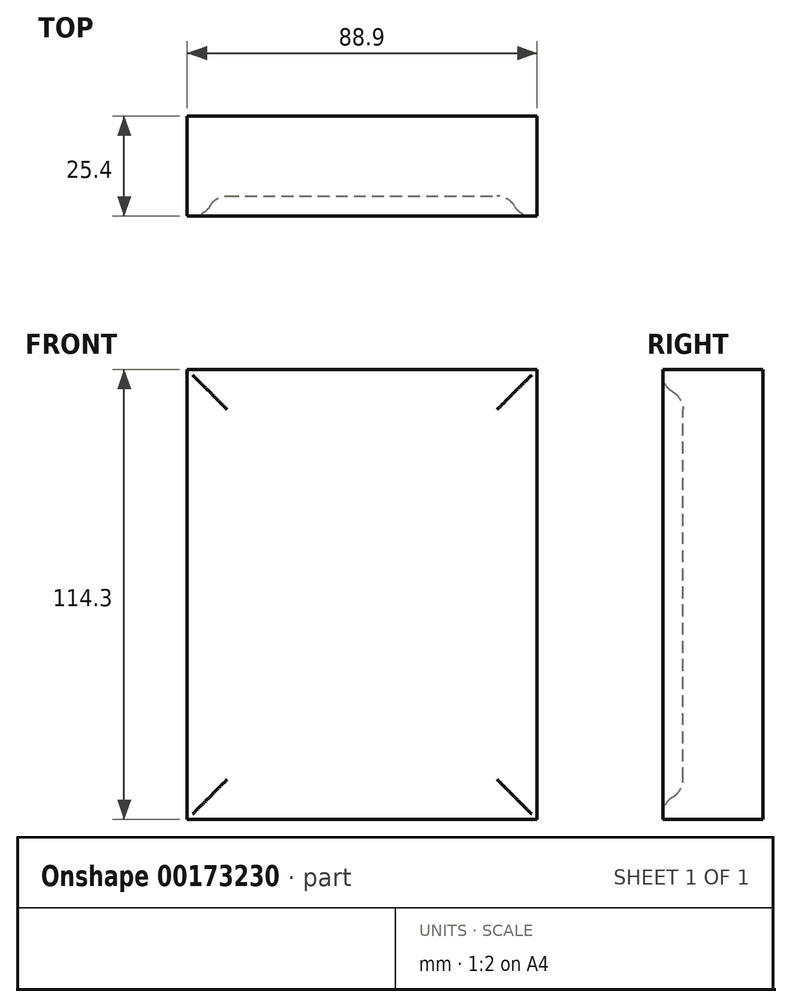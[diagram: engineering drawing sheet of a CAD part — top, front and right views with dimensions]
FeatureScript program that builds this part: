
annotation { "Feature Type Name" : "Feature", "Feature Type Description" : "" }
export const myFeature = defineFeature(function(context is Context, id is Id, definition is map)
    precondition{}
    {
        {
            var Q0;
            Q0=qCreatedBy(makeId("Front.planeOp"),FACE);
            var sketch = newSketch(context, id + "F0", { "sketchPlane" : qUnion([Q0])});
            skLineSegment(sketch, "E0.bottom", {"start": v(0, 0) * mm, "end": v(88.9, 0) * mm});
            skLineSegment(sketch, "E0.top", {"start": v(0, 114.3) * mm, "end": v(88.9, 114.3) * mm});
            skLineSegment(sketch, "E0.left", {"start": v(0, 0) * mm, "end": v(0, 114.3) * mm});
            skLineSegment(sketch, "E0.right", {"start": v(88.9, 0) * mm, "end": v(88.9, 114.3) * mm});
            skSolve(sketch);
        }
        {
            var Q0;
            Q0 = qSketchRegion(id + "F0", true);
            extrude(context, id + "F1", {"entities" : qUnion([Q0]), "depth" : 25.4 * mm});
        }
        {
            var Q0;
            Q0=makeQuery(id+"F1.opExtrude","CAP_FACE",FACE,{"disambiguationData":[OSD([sQuery(id+"F0.wireOp",EDGE,"E0.bottom"),sQuery(id+"F0.wireOp",EDGE,"E0.top"),sQuery(id+"F0.wireOp",EDGE,"E0.left"),sQuery(id+"F0.wireOp",EDGE,"E0.right")])],"isStart":false});
            var sketch = newSketch(context, id + "F2", { "sketchPlane" : qUnion([Q0])});
            skLineSegment(sketch, "E1.bottom", {"start": v(5.08, 5.08) * mm, "end": v(83.82, 5.08) * mm});
            skLineSegment(sketch, "E1.top", {"start": v(5.08, 109.22) * mm, "end": v(83.82, 109.22) * mm});
            skLineSegment(sketch, "E1.left", {"start": v(5.08, 5.08) * mm, "end": v(5.08, 109.22) * mm});
            skLineSegment(sketch, "E1.right", {"start": v(83.82, 5.08) * mm, "end": v(83.82, 109.22) * mm});
            skSolve(sketch);
        }
        {
            var Q0;
            Q0 = qSketchRegion(id + "F2", true);
            extrude(context, id + "F3", {"entities" : qUnion([Q0]), "operationType" : NewBodyOperationType.REMOVE, "oppositeDirection" : true, "depth" : 5.08 * mm});
        }
        {
            var Q0;
            Q0=makeQuery(id+"F3.boolean.opBoolean","COPY",EDGE,{"derivedFrom":makeQuery(id+"F3.opExtrude","CAP_EDGE",EDGE,{"disambiguationData":[OSD([sQuery(id+"F2.wireOp",EDGE,"E1.right")])],"isStart":false})});
            var Q1;
            Q1=makeQuery(id+"F3.boolean.opBoolean","COPY",EDGE,{"derivedFrom":makeQuery(id+"F3.opExtrude","CAP_EDGE",EDGE,{"disambiguationData":[OSD([sQuery(id+"F2.wireOp",EDGE,"E1.top")])],"isStart":false})});
            var Q2;
            Q2=makeQuery(id+"F3.boolean.opBoolean","COPY",EDGE,{"derivedFrom":makeQuery(id+"F3.opExtrude","CAP_EDGE",EDGE,{"disambiguationData":[OSD([sQuery(id+"F2.wireOp",EDGE,"E1.left")])],"isStart":false})});
            var Q3;
            Q3=makeQuery(id+"F3.boolean.opBoolean","COPY",EDGE,{"derivedFrom":makeQuery(id+"F3.opExtrude","CAP_EDGE",EDGE,{"disambiguationData":[OSD([sQuery(id+"F2.wireOp",EDGE,"E1.bottom")])],"isStart":false})});
            fillet(context, id + "F4", {"entities" : qUnion([Q0, Q1, Q2, Q3]), "radius" : 5.08 * mm, "tangentPropagation" : true, "allowEdgeOverflow" : false});
        }
        {
            var Q0;
            Q0=makeQuery(id+"F4.opFillet","BLEND_EDGE",EDGE,{"blendedFrom":[makeQuery(id+"F3.boolean.opBoolean","COPY",EDGE,{"derivedFrom":makeQuery(id+"F3.opExtrude","CAP_EDGE",EDGE,{"disambiguationData":[OSD([sQuery(id+"F2.wireOp",EDGE,"E1.left")])],"isStart":false})}),makeQuery(id+"F1.opExtrude","CAP_FACE",FACE,{"disambiguationData":[OSD([sQuery(id+"F0.wireOp",EDGE,"E0.bottom"),sQuery(id+"F0.wireOp",EDGE,"E0.top"),sQuery(id+"F0.wireOp",EDGE,"E0.left"),sQuery(id+"F0.wireOp",EDGE,"E0.right")])],"isStart":false})],"blendedInto":[makeQuery(id+"F1.opExtrude","CAP_FACE",FACE,{"disambiguationData":[OSD([sQuery(id+"F0.wireOp",EDGE,"E0.bottom"),sQuery(id+"F0.wireOp",EDGE,"E0.top"),sQuery(id+"F0.wireOp",EDGE,"E0.left"),sQuery(id+"F0.wireOp",EDGE,"E0.right")])],"isStart":false})]});
            var Q1;
            Q1=makeQuery(id+"F4.opFillet","BLEND_EDGE",EDGE,{"blendedFrom":[makeQuery(id+"F3.boolean.opBoolean","COPY",EDGE,{"derivedFrom":makeQuery(id+"F3.opExtrude","CAP_EDGE",EDGE,{"disambiguationData":[OSD([sQuery(id+"F2.wireOp",EDGE,"E1.top")])],"isStart":false})}),makeQuery(id+"F1.opExtrude","CAP_FACE",FACE,{"disambiguationData":[OSD([sQuery(id+"F0.wireOp",EDGE,"E0.bottom"),sQuery(id+"F0.wireOp",EDGE,"E0.top"),sQuery(id+"F0.wireOp",EDGE,"E0.left"),sQuery(id+"F0.wireOp",EDGE,"E0.right")])],"isStart":false})],"blendedInto":[makeQuery(id+"F1.opExtrude","CAP_FACE",FACE,{"disambiguationData":[OSD([sQuery(id+"F0.wireOp",EDGE,"E0.bottom"),sQuery(id+"F0.wireOp",EDGE,"E0.top"),sQuery(id+"F0.wireOp",EDGE,"E0.left"),sQuery(id+"F0.wireOp",EDGE,"E0.right")])],"isStart":false})]});
            var Q2;
            Q2=makeQuery(id+"F4.opFillet","BLEND_EDGE",EDGE,{"blendedFrom":[makeQuery(id+"F3.boolean.opBoolean","COPY",EDGE,{"derivedFrom":makeQuery(id+"F3.opExtrude","CAP_EDGE",EDGE,{"disambiguationData":[OSD([sQuery(id+"F2.wireOp",EDGE,"E1.right")])],"isStart":false})}),makeQuery(id+"F1.opExtrude","CAP_FACE",FACE,{"disambiguationData":[OSD([sQuery(id+"F0.wireOp",EDGE,"E0.bottom"),sQuery(id+"F0.wireOp",EDGE,"E0.top"),sQuery(id+"F0.wireOp",EDGE,"E0.left"),sQuery(id+"F0.wireOp",EDGE,"E0.right")])],"isStart":false})],"blendedInto":[makeQuery(id+"F1.opExtrude","CAP_FACE",FACE,{"disambiguationData":[OSD([sQuery(id+"F0.wireOp",EDGE,"E0.bottom"),sQuery(id+"F0.wireOp",EDGE,"E0.top"),sQuery(id+"F0.wireOp",EDGE,"E0.left"),sQuery(id+"F0.wireOp",EDGE,"E0.right")])],"isStart":false})]});
            var Q3;
            Q3=makeQuery(id+"F4.opFillet","BLEND_EDGE",EDGE,{"blendedFrom":[makeQuery(id+"F3.boolean.opBoolean","COPY",EDGE,{"derivedFrom":makeQuery(id+"F3.opExtrude","CAP_EDGE",EDGE,{"disambiguationData":[OSD([sQuery(id+"F2.wireOp",EDGE,"E1.bottom")])],"isStart":false})}),makeQuery(id+"F1.opExtrude","CAP_FACE",FACE,{"disambiguationData":[OSD([sQuery(id+"F0.wireOp",EDGE,"E0.bottom"),sQuery(id+"F0.wireOp",EDGE,"E0.top"),sQuery(id+"F0.wireOp",EDGE,"E0.left"),sQuery(id+"F0.wireOp",EDGE,"E0.right")])],"isStart":false})],"blendedInto":[makeQuery(id+"F1.opExtrude","CAP_FACE",FACE,{"disambiguationData":[OSD([sQuery(id+"F0.wireOp",EDGE,"E0.bottom"),sQuery(id+"F0.wireOp",EDGE,"E0.top"),sQuery(id+"F0.wireOp",EDGE,"E0.left"),sQuery(id+"F0.wireOp",EDGE,"E0.right")])],"isStart":false})]});
            fillet(context, id + "F5", {"entities" : qUnion([Q0, Q1, Q2, Q3]), "radius" : 5.08 * mm, "tangentPropagation" : true, "allowEdgeOverflow" : false});
        }
    });
